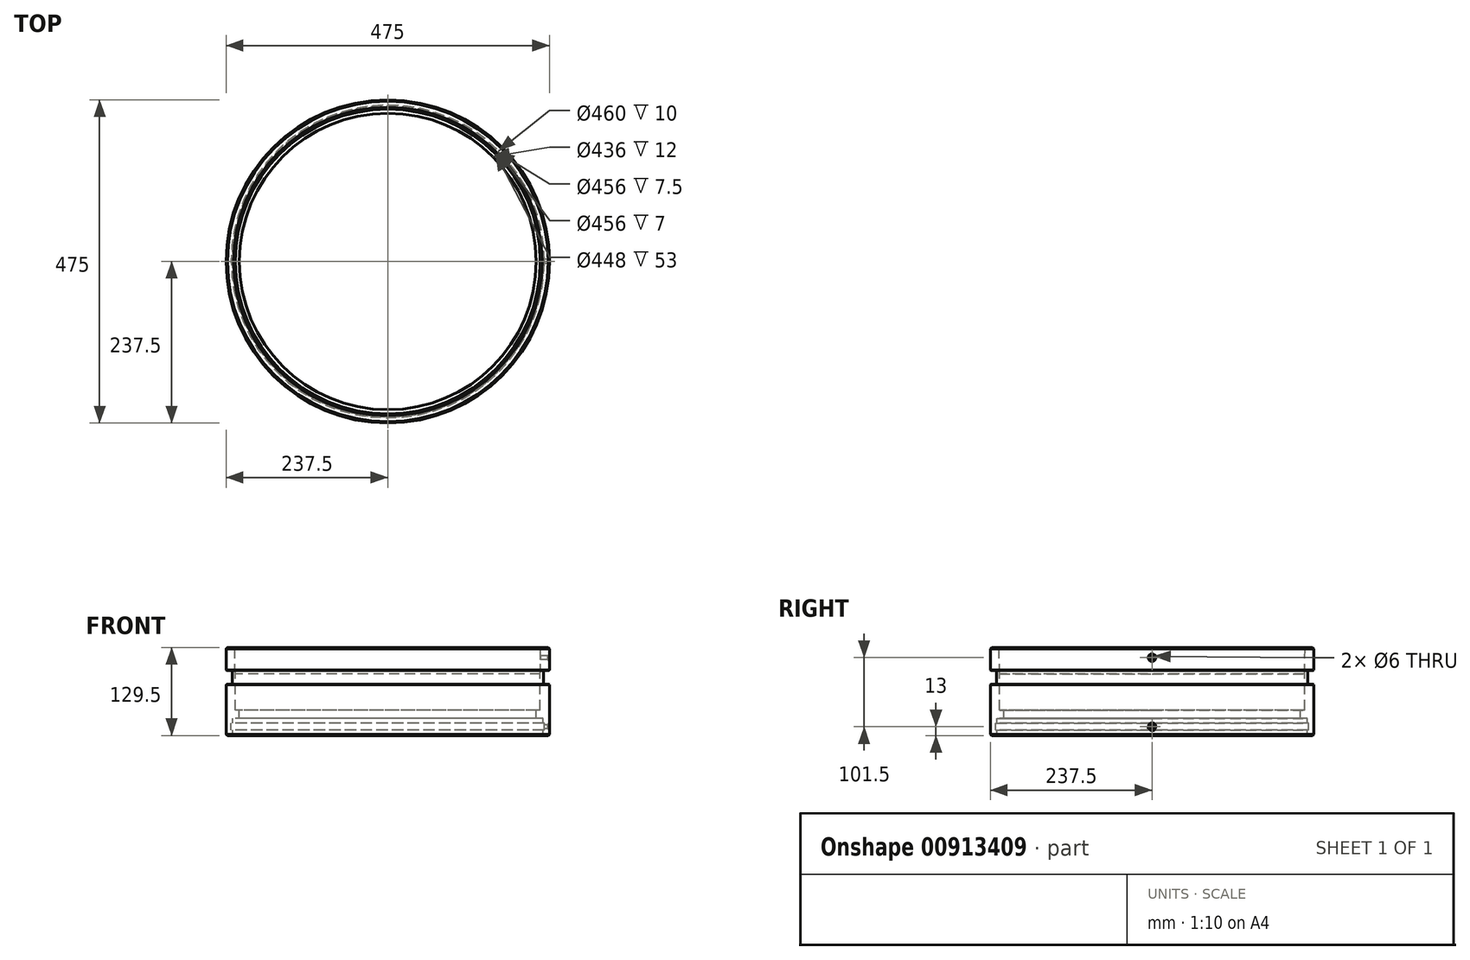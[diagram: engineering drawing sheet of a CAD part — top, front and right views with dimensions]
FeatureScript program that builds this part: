
annotation { "Feature Type Name" : "Feature", "Feature Type Description" : "" }
export const myFeature = defineFeature(function(context is Context, id is Id, definition is map)
    precondition{}
    {
        {
            var Q0;
            Q0=qCreatedBy(makeId("Front.planeOp"),FACE);
            var sketch = newSketch(context, id + "F0", { "sketchPlane" : qUnion([Q0])});
            skLineSegment(sketch, "E0", {"start": v(0, 147.96) * mm, "end": v(0, -93.78) * mm, "construction": true});
            skLineSegment(sketch, "E1", {"start": v(237.5, 0) * mm, "end": v(237.5, 75.5) * mm});
            skLineSegment(sketch, "E2", {"start": v(237.5, 75.5) * mm, "end": v(228.5, 75.5) * mm});
            skLineSegment(sketch, "E3", {"start": v(228.5, 75.5) * mm, "end": v(228.5, 95.5) * mm});
            skLineSegment(sketch, "E4", {"start": v(228.5, 95.5) * mm, "end": v(237.5, 95.5) * mm});
            skLineSegment(sketch, "E5", {"start": v(237.5, 95.5) * mm, "end": v(237.5, 129.5) * mm});
            skLineSegment(sketch, "E6", {"start": v(237.5, 129.5) * mm, "end": v(224.68, 129.5) * mm});
            skLineSegment(sketch, "E7", {"start": v(237.5, 0) * mm, "end": v(228, 0) * mm});
            skLineSegment(sketch, "E8", {"start": v(224.68, 129.5) * mm, "end": v(224, 90.5) * mm});
            skLineSegment(sketch, "E9", {"start": v(224, 37.5) * mm, "end": v(218, 37.5) * mm});
            skLineSegment(sketch, "E10", {"start": v(218, 37.5) * mm, "end": v(218, 25.5) * mm});
            skLineSegment(sketch, "E11", {"start": v(218, 25.5) * mm, "end": v(228, 25.5) * mm});
            skLineSegment(sketch, "E12", {"start": v(228, 25.5) * mm, "end": v(228, 18) * mm});
            skLineSegment(sketch, "E13", {"start": v(228, 18) * mm, "end": v(230, 18) * mm});
            skLineSegment(sketch, "E14", {"start": v(230, 18) * mm, "end": v(230, 8) * mm});
            skLineSegment(sketch, "E15", {"start": v(230, 8) * mm, "end": v(228, 8) * mm});
            skLineSegment(sketch, "E16", {"start": v(228, 8) * mm, "end": v(228, 0) * mm});
            skLineSegment(sketch, "E17", {"start": v(224, 37.5) * mm, "end": v(224, 90.5) * mm});
            skPoint(sketch, "E18.orphan", {"position": v(0, 129.5) * mm});
            skSolve(sketch);
        }
        {
            var Q0;
            Q0=makeQuery(id+"F0.imprint","IMPRINT",FACE,{"disambiguationData":[TD([[makeQuery(id+"F0.imprint","IMPRINT",EDGE,{"derivedFrom":sQuery(id+"F0.wireOp",EDGE,"E1")}),1.0]])]});
            var Q1;
            Q1=sQuery(id+"F0.wireOp",EDGE,"E0");
            revolve(context, id + "F1", {"surfaceOperationType" : NewSurfaceOperationType.NEW, "entities" : qUnion([Q0]), "axis" : qUnion([Q1]), "revolveType" : RevolveType.FULL});
        }
        {
            var Q0;
            Q0=makeQuery(id+"F1.opRevolve","SWEPT_EDGE",EDGE,{"disambiguationData":[OSD([sQuery(id+"F0.wireOp",EDGE,"E4"),sQuery(id+"F0.wireOp",EDGE,"E5")])]});
            var Q1;
            Q1=makeQuery(id+"F1.opRevolve","SWEPT_EDGE",EDGE,{"disambiguationData":[OSD([sQuery(id+"F0.wireOp",EDGE,"E1"),sQuery(id+"F0.wireOp",EDGE,"E2")])]});
            var Q2;
            Q2=makeQuery(id+"F1.opRevolve","SWEPT_EDGE",EDGE,{"disambiguationData":[OSD([sQuery(id+"F0.wireOp",EDGE,"E7"),sQuery(id+"F0.wireOp",EDGE,"E16")])]});
            chamfer(context, id + "F2", {"entities" : qUnion([Q0, Q1, Q2]), "width" : 1 * mm, "tangentPropagation" : true});
        }
        {
            var Q0;
            Q0=makeQuery(id+"F1.opRevolve","SWEPT_EDGE",EDGE,{"disambiguationData":[OSD([sQuery(id+"F0.wireOp",EDGE,"E6"),sQuery(id+"F0.wireOp",EDGE,"E8")])]});
            var Q1;
            Q1=makeQuery(id+"F1.opRevolve","SWEPT_EDGE",EDGE,{"disambiguationData":[OSD([sQuery(id+"F0.wireOp",EDGE,"E5"),sQuery(id+"F0.wireOp",EDGE,"E6")])]});
            var Q2;
            Q2=makeQuery(id+"F1.opRevolve","SWEPT_EDGE",EDGE,{"disambiguationData":[OSD([sQuery(id+"F0.wireOp",EDGE,"E1"),sQuery(id+"F0.wireOp",EDGE,"E7")])]});
            chamfer(context, id + "F3", {"entities" : qUnion([Q0, Q1, Q2]), "width" : 2 * mm, "tangentPropagation" : true});
        }
        {
            var Q0;
            Q0=qCreatedBy(makeId("Front.planeOp"),FACE);
            var sketch = newSketch(context, id + "F4", { "sketchPlane" : qUnion([Q0])});
            skLineSegment(sketch, "E19", {"start": v(270.84, 0) * mm, "end": v(173.87, 0) * mm, "construction": true});
            skLineSegment(sketch, "E20.0", {"start": v(270.84, 129.5) * mm, "end": v(173.87, 129.5) * mm, "construction": true});
            skLineSegment(sketch, "E21.0", {"start": v(270.84, 114.5) * mm, "end": v(173.87, 114.5) * mm, "construction": true});
            skLineSegment(sketch, "E22.0", {"start": v(270.84, 13) * mm, "end": v(173.87, 13) * mm, "construction": true});
            skLineSegment(sketch, "E23.0", {"start": v(234.9, 111.5) * mm, "end": v(222.32, 111.5) * mm});
            skLineSegment(sketch, "E24", {"start": v(0, -10.21) * mm, "end": v(0, 140.78) * mm, "construction": true});
            skLineSegment(sketch, "E25.0", {"start": v(237.5, -10.21) * mm, "end": v(237.5, 13) * mm});
            skLineSegment(sketch, "E26.0", {"start": v(234.9, 111.5) * mm, "end": v(234.9, 140.78) * mm});
            skLineSegment(sketch, "E27", {"start": v(234.9, 111.5) * mm, "end": v(237.5, 108.9) * mm});
            skLineSegment(sketch, "E28.filletArc", {"start": v(234.9, 111.5) * mm, "end": v(234.9, 111.5) * mm});
            skLineSegment(sketch, "E29", {"start": v(222.32, 111.5) * mm, "end": v(222.32, 114.5) * mm});
            skLineSegment(sketch, "E30", {"start": v(222.32, 114.5) * mm, "end": v(237.5, 114.5) * mm});
            skLineSegment(sketch, "E31", {"start": v(237.5, 114.5) * mm, "end": v(237.5, 108.9) * mm});
            skLineSegment(sketch, "E32.trimOffspring", {"start": v(237.5, 108.9) * mm, "end": v(237.5, 114.5) * mm});
            skLineSegment(sketch, "E33.trimOffspring", {"start": v(237.5, 129.5) * mm, "end": v(237.5, 140.78) * mm});
            skLineSegment(sketch, "E34.0", {"start": v(270.84, 63.75) * mm, "end": v(173.87, 63.75) * mm, "construction": true});
            skLineSegment(sketch, "E35.MirrorCS", {"start": v(234.9, 16) * mm, "end": v(237.5, 18.6) * mm});
            skLineSegment(sketch, "E36.MirrorCS", {"start": v(222.32, 16) * mm, "end": v(222.32, 13) * mm});
            skLineSegment(sketch, "E37.MirrorCS", {"start": v(237.5, 13) * mm, "end": v(237.5, 18.6) * mm});
            skLineSegment(sketch, "E38.MirrorCS", {"start": v(237.5, 18.6) * mm, "end": v(237.5, 13) * mm});
            skLineSegment(sketch, "E39.MirrorCS", {"start": v(234.9, 16) * mm, "end": v(234.9, 16) * mm});
            skLineSegment(sketch, "E40.MirrorCS", {"start": v(234.9, 16) * mm, "end": v(222.32, 16) * mm});
            skLineSegment(sketch, "E41.MirrorCS", {"start": v(222.32, 13) * mm, "end": v(237.5, 13) * mm});
            skSolve(sketch);
        }
        {
            var Q0;
            {var subQ0=sQuery(id+"F4.wireOp",EDGE,"E23.0");Q0=makeQuery(id+"F4.imprint","IMPRINT",FACE,{"disambiguationData":[TD([[makeQuery(id+"F4.imprint","IMPRINT",EDGE,{"derivedFrom":subQ0}),-1.0]])]});}
            var Q1;
            {var subQ0=sQuery(id+"F4.wireOp",EDGE,"E27");Q1=makeQuery(id+"F4.imprint","IMPRINT",FACE,{"disambiguationData":[TD([[makeQuery(id+"F4.imprint","IMPRINT",EDGE,{"derivedFrom":subQ0}),1.0]])]});}
            var Q2;
            Q2=sQuery(id+"F4.wireOp",EDGE,"E21.0");
            revolve(context, id + "F5", {"operationType" : NewBodyOperationType.REMOVE, "surfaceOperationType" : NewSurfaceOperationType.NEW, "entities" : qUnion([Q0, Q1]), "axis" : qUnion([Q2]), "revolveType" : RevolveType.FULL, "oppositeDirection" : true});
        }
        {
            var Q0;
            Q0=makeQuery(id+"F4.imprint","IMPRINT",FACE,{"disambiguationData":[TD([[makeQuery(id+"F4.imprint","IMPRINT",EDGE,{"derivedFrom":sQuery(id+"F4.wireOp",EDGE,"E35.MirrorCS")}),-1.0]])]});
            var Q1;
            Q1=sQuery(id+"F4.wireOp",EDGE,"E22.0");
            revolve(context, id + "F6", {"operationType" : NewBodyOperationType.REMOVE, "surfaceOperationType" : NewSurfaceOperationType.NEW, "entities" : qUnion([Q0]), "axis" : qUnion([Q1]), "revolveType" : RevolveType.FULL, "oppositeDirection" : true});
        }
    });
